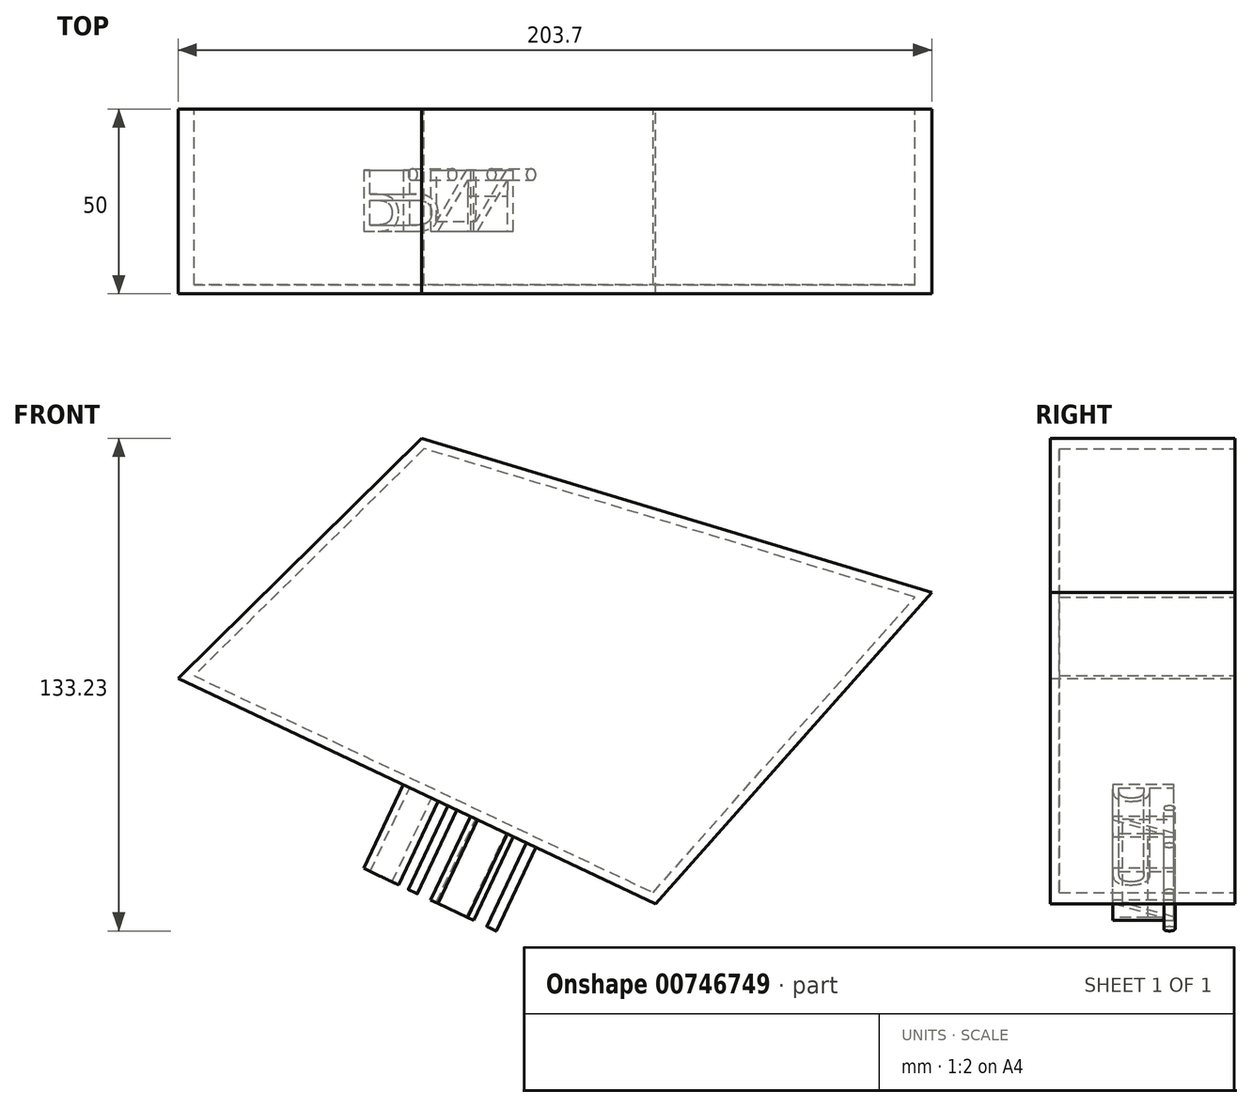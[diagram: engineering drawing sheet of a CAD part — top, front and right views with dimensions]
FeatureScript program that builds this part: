
annotation { "Feature Type Name" : "Feature", "Feature Type Description" : "" }
export const myFeature = defineFeature(function(context is Context, id is Id, definition is map)
    precondition{}
    {
        {
            var Q0;
            Q0=qCreatedBy(makeId("Front.planeOp"),FACE);
            var sketch = newSketch(context, id + "F0", { "sketchPlane" : qUnion([Q0])});
            skLineSegment(sketch, "E0", {"start": v(-273.95, -68.9) * mm, "end": v(-144.94, -129.85) * mm});
            skLineSegment(sketch, "E1", {"start": v(-144.94, -129.85) * mm, "end": v(-70.25, -45.61) * mm});
            skLineSegment(sketch, "E2", {"start": v(-70.25, -45.61) * mm, "end": v(-208.14, -3.94) * mm});
            skLineSegment(sketch, "E3", {"start": v(-208.14, -3.94) * mm, "end": v(-273.95, -68.9) * mm});
            skSolve(sketch);
        }
        {
            var Q0;
            Q0 = qSketchRegion(id + "F0", true);
            extrude(context, id + "F1", {"entities" : qUnion([Q0]), "depth" : 50 * mm, "offsetDistance" : 25 * mm});
        }
        {
            var Q0;
            Q0=makeQuery(id+"F1.opExtrude","CAP_FACE",FACE,{"disambiguationData":[OSD([sQuery(id+"F0.wireOp",EDGE,"E0"),sQuery(id+"F0.wireOp",EDGE,"E1"),sQuery(id+"F0.wireOp",EDGE,"E2"),sQuery(id+"F0.wireOp",EDGE,"E3")])],"isStart":true});
            shell(context, id + "F2", {"entities" : qUnion([Q0]), "thickness" : 2.5 * mm});
        }
        {
            var Q0;
            Q0=makeQuery(id+"F1.opExtrude","SWEPT_FACE",FACE,{"disambiguationData":[OSD([sQuery(id+"F0.wireOp",EDGE,"E0")])]});
            var sketch = newSketch(context, id + "F3", { "sketchPlane" : qUnion([Q0])});
            skText(sketch, "E4", { "text": "P.N.", "fontName": "OpenSans-Regular.ttf"});
            const initialGuessF3  = {"E4": [-0.15321, 0.01654, 1, 0, 0.01661]};
            skSetInitialGuess(sketch, initialGuessF3);
            skSolve(sketch);
        }
        {
            var Q0;
            Q0 = qSketchRegion(id + "F3", true);
            extrude(context, id + "F4", {"entities" : qUnion([Q0]), "operationType" : NewBodyOperationType.ADD, "depth" : 25 * mm, "offsetDistance" : 25 * mm});
        }
    });
